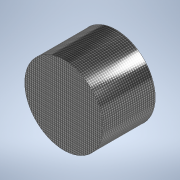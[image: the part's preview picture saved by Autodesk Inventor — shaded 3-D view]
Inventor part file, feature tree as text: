
AUTODESK INVENTOR PART (.ipt)
format: ipt  version: 2020 (Build 240168000, 168)  size: 120,832 bytes
history: native  units: mm
features: extrude x1, sketch x1
ambient origin geometry x8: Origin, YZ Plane, XZ Plane, XY Plane, X Axis, Y Axis, Z Axis, Center Point
bodies: Solid1 (feature_tree)
feature tree (2):
  extrude  "Extrusion1"  Depth=50.0mm TaperAngle=0.0deg
  sketch  "Sketch1"  dims[d0=75.0mm d1=50.0mm d2=0.0mm]
